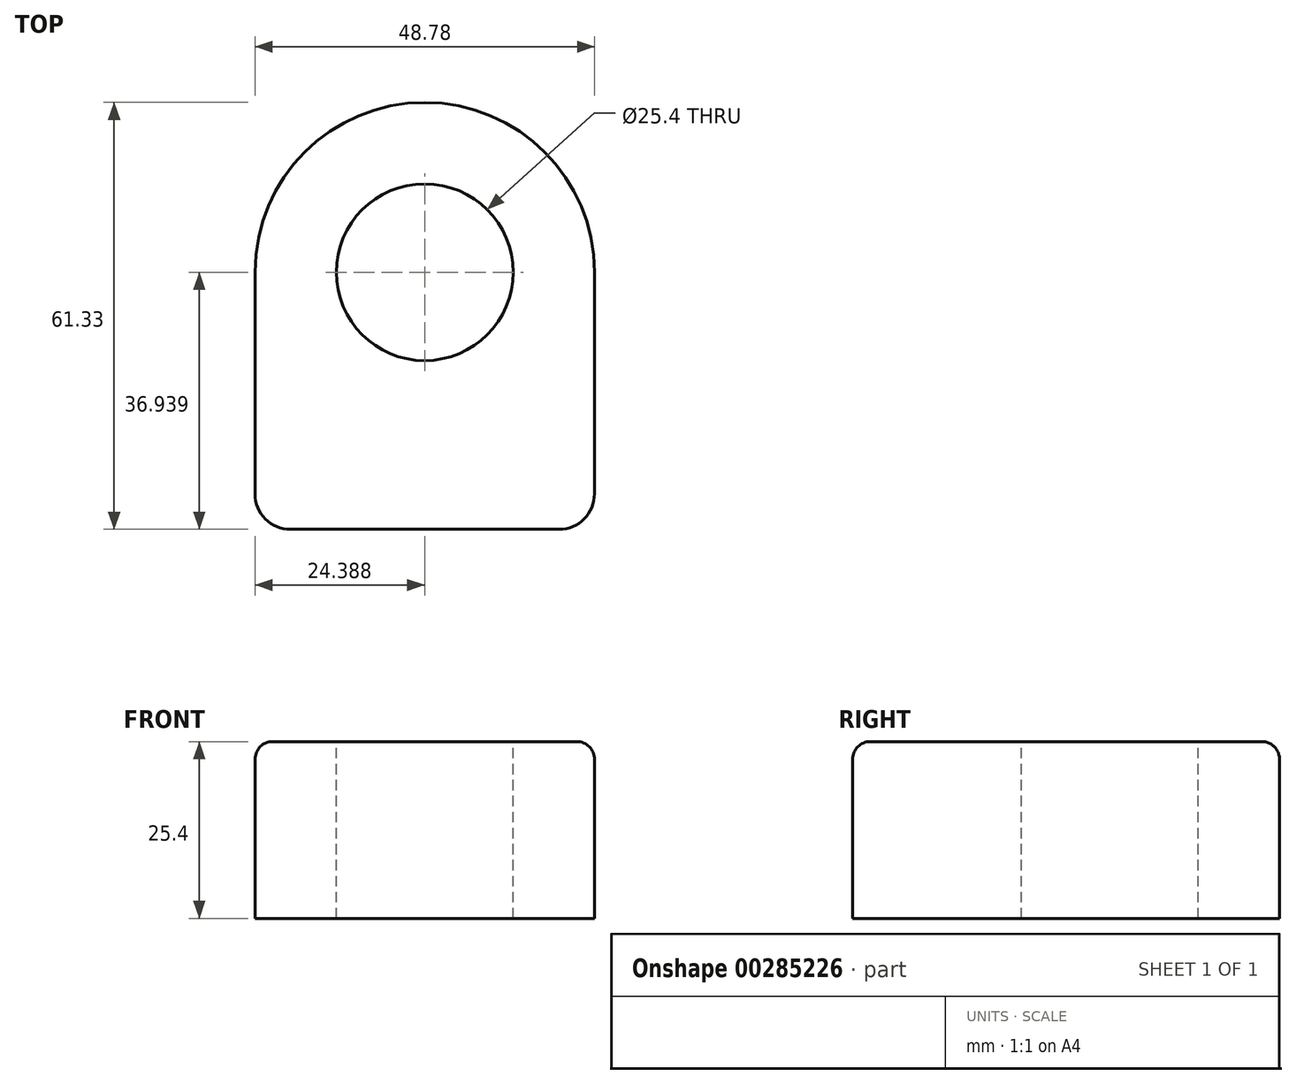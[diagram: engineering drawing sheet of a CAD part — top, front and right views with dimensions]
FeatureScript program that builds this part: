
annotation { "Feature Type Name" : "Feature", "Feature Type Description" : "" }
export const myFeature = defineFeature(function(context is Context, id is Id, definition is map)
    precondition{}
    {
        {
            var Q0;
            Q0=qCreatedBy(makeId("Top.planeOp"),FACE);
            var sketch = newSketch(context, id + "F0", { "sketchPlane" : qUnion([Q0])});
            skLineSegment(sketch, "E0.bottom", {"start": v(0, 0) * mm, "end": v(48.78, 0) * mm});
            skLineSegment(sketch, "E0.left", {"start": v(0, 0) * mm, "end": v(0, 36.94) * mm});
            skLineSegment(sketch, "E0.right", {"start": v(48.78, 0) * mm, "end": v(48.78, 36.94) * mm});
            skArc(sketch, "E1", {"start": v(48.78, 36.94) * mm, "mid": v(24.39, 61.33) * mm, "end": v(0, 36.94) * mm});
            skSolve(sketch);
        }
        {
            var Q0;
            Q0=qSketchRegion(id+"F0",true);
            extrude(context, id + "F1", {"entities" : qUnion([Q0]), "depth" : 25.4 * mm});
        }
        {
            var Q0;
            Q0=makeQuery(id+"F1.opExtrude","CAP_FACE",FACE,{"disambiguationData":[OSD([sQuery(id+"F0.wireOp",EDGE,"E0.bottom"),sQuery(id+"F0.wireOp",EDGE,"E0.left"),sQuery(id+"F0.wireOp",EDGE,"E0.right"),sQuery(id+"F0.wireOp",EDGE,"E1")])],"isStart":false});
            var sketch = newSketch(context, id + "F2", { "sketchPlane" : qUnion([Q0])});
            skCircle(sketch, "E2", {"center": v(24.39, 36.94) * mm, "radius": 12.7 * mm});
            skSolve(sketch);
        }
        {
            var Q0;
            Q0=sQuery(id+"F2.wireOp",VERTEX,"E2.center");
            var Q1;
            Q1=makeQuery(id+"F1.opExtrude","SWEPT_BODY",BODY,{"disambiguationData":[OSD([sQuery(id+"F0.wireOp",EDGE,"E0.bottom"),sQuery(id+"F0.wireOp",EDGE,"E0.left"),sQuery(id+"F0.wireOp",EDGE,"E0.right"),sQuery(id+"F0.wireOp",EDGE,"E1")])]});
            hole(context, id + "F3", {"style" : HoleStyle.SIMPLE, "endStyle" : HoleEndStyle.THROUGH, "holeDiameter" : 25.4 * mm, "tappedDepth" : 12.7 * mm, "tapClearance" : 3, "locations" : qUnion([Q0]), "scope" : qUnion([Q1])});
        }
        {
            var Q0;
            Q0=makeQuery(id+"F1.opExtrude","CAP_EDGE",EDGE,{"disambiguationData":[OSD([sQuery(id+"F0.wireOp",EDGE,"E0.bottom")])],"isStart":false});
            var Q1;
            Q1=makeQuery(id+"F1.opExtrude","CAP_EDGE",EDGE,{"disambiguationData":[OSD([sQuery(id+"F0.wireOp",EDGE,"E0.right")])],"isStart":false});
            fillet(context, id + "F4", {"entities" : qUnion([Q0, Q1]), "radius" : 2.54 * mm, "tangentPropagation" : true, "allowEdgeOverflow" : false});
        }
        {
            var Q0;
            Q0=makeQuery(id+"F1.opExtrude","SWEPT_EDGE",EDGE,{"disambiguationData":[OSD([sQuery(id+"F0.wireOp",EDGE,"E0.bottom"),sQuery(id+"F0.wireOp",EDGE,"E0.right")])]});
            var Q1;
            Q1=makeQuery(id+"F1.opExtrude","SWEPT_EDGE",EDGE,{"disambiguationData":[OSD([sQuery(id+"F0.wireOp",EDGE,"E0.bottom"),sQuery(id+"F0.wireOp",EDGE,"E0.left")])]});
            fillet(context, id + "F5", {"entities" : qUnion([Q0, Q1]), "radius" : 5.08 * mm, "tangentPropagation" : true, "allowEdgeOverflow" : false});
        }
    });
